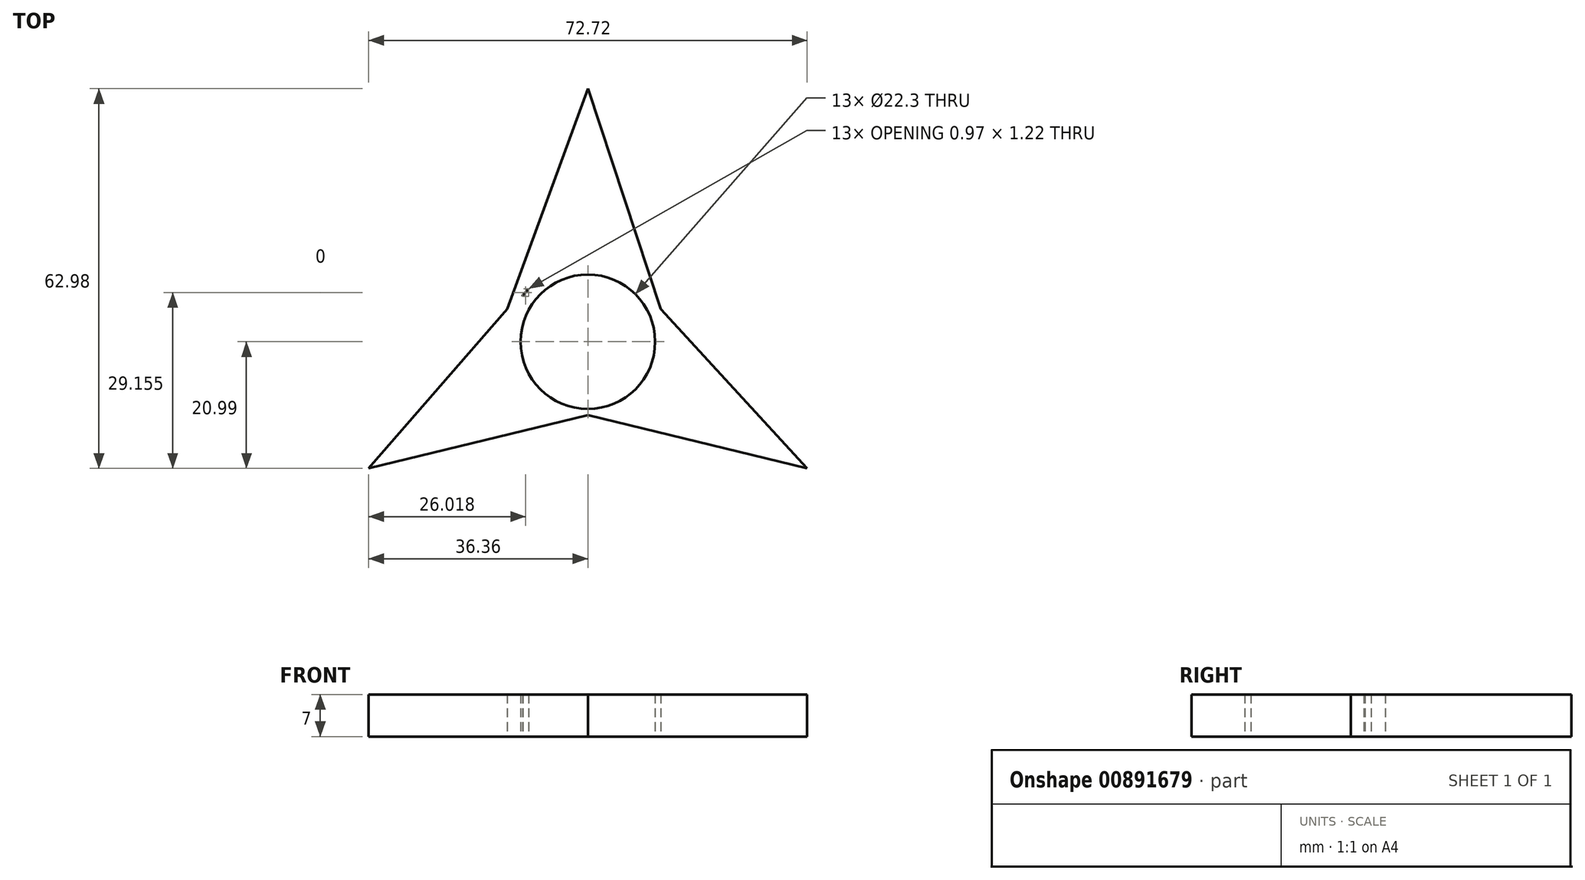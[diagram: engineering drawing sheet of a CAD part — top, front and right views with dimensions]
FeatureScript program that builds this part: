
annotation { "Feature Type Name" : "Feature", "Feature Type Description" : "" }
export const myFeature = defineFeature(function(context is Context, id is Id, definition is map)
    precondition{}
    {
        {
            var Q0;
            Q0=qCreatedBy(makeId("Top.planeOp"),FACE);
            var sketch = newSketch(context, id + "F0", { "sketchPlane" : qUnion([Q0])});
            skCircle(sketch, "E0", {"center": v(0, 0) * mm, "radius": 11.15 * mm});
            skLineSegment(sketch, "E1", {"start": v(-10.83, 7.55) * mm, "end": v(-10.76, 7.77) * mm});
            skLineSegment(sketch, "E2", {"start": v(0, 41.99) * mm, "end": v(12.1, 5.43) * mm});
            skLineSegment(sketch, "E3.1.1", {"start": v(-10.76, 7.77) * mm, "end": v(-9.86, 8.78) * mm});
            skLineSegment(sketch, "E3.2.0", {"start": v(11.95, 5.6) * mm, "end": v(12.1, 5.43) * mm});
            skArc(sketch, "E4.trimOffspring", {"start": v(-9.86, 8.78) * mm, "mid": v(-10.36, 8.18) * mm, "end": v(-10.83, 7.55) * mm});
            skPoint(sketch, "E5.orphan", {"position": v(-13.2, 0) * mm});
            skPoint(sketch, "E6.orphan", {"position": v(-6.95, 12.04) * mm});
            skPoint(sketch, "E7.orphan", {"position": v(6.6, 11.43) * mm});
            skPoint(sketch, "E8.orphan", {"position": v(6.6, -11.43) * mm});
            skPoint(sketch, "E9.orphan", {"position": v(-6.95, -12.04) * mm});
            skPoint(sketch, "E10.orphan", {"position": v(13.9, 0) * mm});
            skLineSegment(sketch, "E11", {"start": v(12.1, 5.43) * mm, "end": v(36.36, -21) * mm});
            skLineSegment(sketch, "E12", {"start": v(-13.38, 5.43) * mm, "end": v(-36.36, -21) * mm});
            skLineSegment(sketch, "E13", {"start": v(-13.38, 5.43) * mm, "end": v(0, 41.99) * mm});
            skLineSegment(sketch, "E14", {"start": v(0, -12.17) * mm, "end": v(-36.36, -21) * mm});
            skLineSegment(sketch, "E15", {"start": v(0, -12.17) * mm, "end": v(36.36, -21) * mm});
            skSolve(sketch);
        }
        {
            var Q0;
            Q0=makeQuery(id+"F0.imprint","IMPRINT",FACE,{"disambiguationData":[TD([[makeQuery(id+"F0.imprint","IMPRINT",EDGE,{"derivedFrom":sQuery(id+"F0.wireOp",EDGE,"E0")}),-1.0]])]});
            extrude(context, id + "F1", {"entities" : qUnion([Q0]), "depth" : 7 * mm, "offsetDistance" : 25 * mm});
        }
    });
